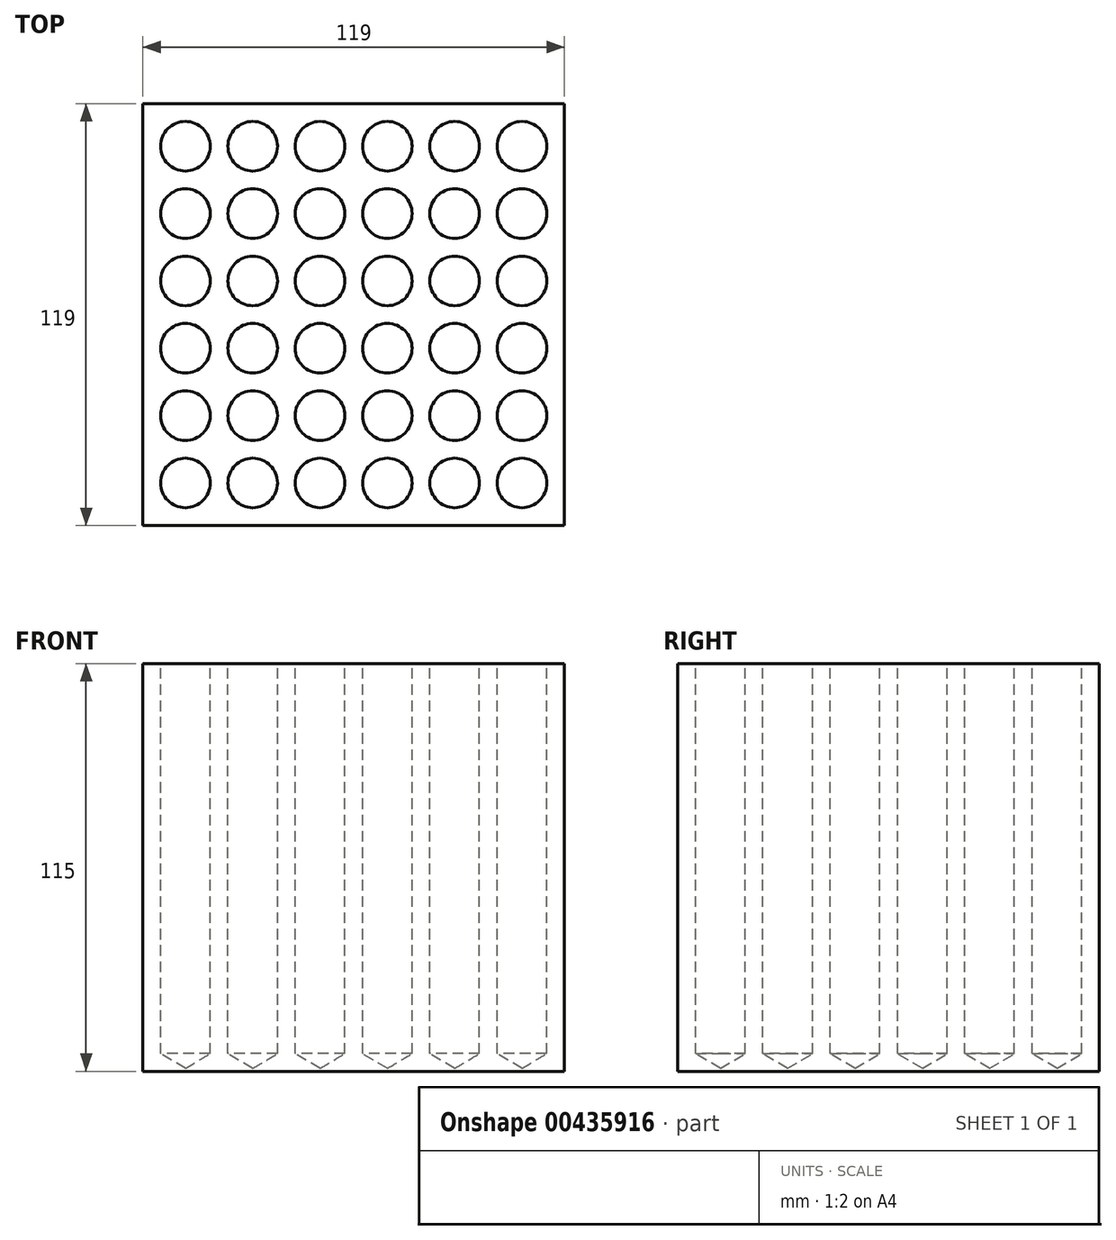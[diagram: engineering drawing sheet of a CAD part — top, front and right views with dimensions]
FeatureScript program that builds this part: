
annotation { "Feature Type Name" : "Feature", "Feature Type Description" : "" }
export const myFeature = defineFeature(function(context is Context, id is Id, definition is map)
    precondition{}
    {
        {
            var Q0;
            Q0=qCreatedBy(makeId("Top.planeOp"),FACE);
            var sketch = newSketch(context, id + "F0", { "sketchPlane" : qUnion([Q0])});
            skLineSegment(sketch, "E0.bottom", {"start": v(-97.3, 0) * mm, "end": v(21.7, 0) * mm});
            skLineSegment(sketch, "E0.top", {"start": v(-97.3, -119) * mm, "end": v(21.7, -119) * mm});
            skLineSegment(sketch, "E0.left", {"start": v(-97.3, 0) * mm, "end": v(-97.3, -119) * mm});
            skLineSegment(sketch, "E0.right", {"start": v(21.7, 0) * mm, "end": v(21.7, -119) * mm});
            skPoint(sketch, "E1", {"position": v(-85.3, -12) * mm});
            skPoint(sketch, "E2.0.1.0", {"position": v(-85.3, -31) * mm});
            skPoint(sketch, "E2.0.2.0", {"position": v(-85.3, -50) * mm});
            skPoint(sketch, "E2.0.3.0", {"position": v(-85.3, -69) * mm});
            skPoint(sketch, "E2.0.4.0", {"position": v(-85.3, -88) * mm});
            skPoint(sketch, "E2.0.5.0", {"position": v(-85.3, -107) * mm});
            skPoint(sketch, "E2.1.0.0", {"position": v(-66.3, -12) * mm});
            skPoint(sketch, "E2.1.1.0", {"position": v(-66.3, -31) * mm});
            skPoint(sketch, "E2.1.2.0", {"position": v(-66.3, -50) * mm});
            skPoint(sketch, "E2.1.3.0", {"position": v(-66.3, -69) * mm});
            skPoint(sketch, "E2.1.4.0", {"position": v(-66.3, -88) * mm});
            skPoint(sketch, "E2.1.5.0", {"position": v(-66.3, -107) * mm});
            skPoint(sketch, "E2.2.0.0", {"position": v(-47.3, -12) * mm});
            skPoint(sketch, "E2.2.1.0", {"position": v(-47.3, -31) * mm});
            skPoint(sketch, "E2.2.2.0", {"position": v(-47.3, -50) * mm});
            skPoint(sketch, "E2.2.3.0", {"position": v(-47.3, -69) * mm});
            skPoint(sketch, "E2.2.4.0", {"position": v(-47.3, -88) * mm});
            skPoint(sketch, "E2.2.5.0", {"position": v(-47.3, -107) * mm});
            skPoint(sketch, "E2.3.0.0", {"position": v(-28.3, -12) * mm});
            skPoint(sketch, "E2.3.1.0", {"position": v(-28.3, -31) * mm});
            skPoint(sketch, "E2.3.2.0", {"position": v(-28.3, -50) * mm});
            skPoint(sketch, "E2.3.3.0", {"position": v(-28.3, -69) * mm});
            skPoint(sketch, "E2.3.4.0", {"position": v(-28.3, -88) * mm});
            skPoint(sketch, "E2.3.5.0", {"position": v(-28.3, -107) * mm});
            skPoint(sketch, "E2.4.0.0", {"position": v(-9.3, -12) * mm});
            skPoint(sketch, "E2.4.1.0", {"position": v(-9.3, -31) * mm});
            skPoint(sketch, "E2.4.2.0", {"position": v(-9.3, -50) * mm});
            skPoint(sketch, "E2.4.3.0", {"position": v(-9.3, -69) * mm});
            skPoint(sketch, "E2.4.4.0", {"position": v(-9.3, -88) * mm});
            skPoint(sketch, "E2.4.5.0", {"position": v(-9.3, -107) * mm});
            skPoint(sketch, "E2.5.0.0", {"position": v(9.7, -12) * mm});
            skPoint(sketch, "E2.5.1.0", {"position": v(9.7, -31) * mm});
            skPoint(sketch, "E2.5.2.0", {"position": v(9.7, -50) * mm});
            skPoint(sketch, "E2.5.3.0", {"position": v(9.7, -69) * mm});
            skPoint(sketch, "E2.5.4.0", {"position": v(9.7, -88) * mm});
            skPoint(sketch, "E2.5.5.0", {"position": v(9.7, -107) * mm});
            skLineSegment(sketch, "E2.direction1", {"start": v(-85.3, -12) * mm, "end": v(-66.3, -12) * mm, "construction": true});
            skLineSegment(sketch, "E2.direction2", {"start": v(-85.3, -12) * mm, "end": v(-85.3, -31) * mm, "construction": true});
            skSolve(sketch);
        }
        {
            var Q0;
            Q0=makeQuery(id+"F0.imprint","IMPRINT",FACE,{"disambiguationData":[TD([[makeQuery(id+"F0.imprint","IMPRINT",EDGE,{"derivedFrom":sQuery(id+"F0.wireOp",EDGE,"E0.bottom")}),-1.0]])]});
            extrude(context, id + "F1", {"entities" : qUnion([Q0]), "oppositeDirection" : true, "depth" : 115 * mm});
        }
        {
            var Q0;
            Q0=sQuery(id+"F0.wireOp",VERTEX,"E1");
            var Q1;
            Q1=sQuery(id+"F0.wireOp",VERTEX,"E2.1.0.0");
            var Q2;
            Q2=sQuery(id+"F0.wireOp",VERTEX,"E2.2.0.0");
            var Q3;
            Q3=sQuery(id+"F0.wireOp",VERTEX,"E2.3.0.0");
            var Q4;
            Q4=sQuery(id+"F0.wireOp",VERTEX,"E2.4.0.0");
            var Q5;
            Q5=sQuery(id+"F0.wireOp",VERTEX,"E2.5.0.0");
            var Q6;
            Q6=sQuery(id+"F0.wireOp",VERTEX,"E2.5.1.0");
            var Q7;
            Q7=sQuery(id+"F0.wireOp",VERTEX,"E2.4.1.0");
            var Q8;
            Q8=sQuery(id+"F0.wireOp",VERTEX,"E2.3.1.0");
            var Q9;
            Q9=sQuery(id+"F0.wireOp",VERTEX,"E2.2.1.0");
            var Q10;
            Q10=sQuery(id+"F0.wireOp",VERTEX,"E2.1.1.0");
            var Q11;
            Q11=sQuery(id+"F0.wireOp",VERTEX,"E2.0.1.0");
            var Q12;
            Q12=sQuery(id+"F0.wireOp",VERTEX,"E2.0.2.0");
            var Q13;
            Q13=sQuery(id+"F0.wireOp",VERTEX,"E2.1.2.0");
            var Q14;
            Q14=sQuery(id+"F0.wireOp",VERTEX,"E2.2.2.0");
            var Q15;
            Q15=sQuery(id+"F0.wireOp",VERTEX,"E2.3.2.0");
            var Q16;
            Q16=sQuery(id+"F0.wireOp",VERTEX,"E2.4.2.0");
            var Q17;
            Q17=sQuery(id+"F0.wireOp",VERTEX,"E2.5.2.0");
            var Q18;
            Q18=sQuery(id+"F0.wireOp",VERTEX,"E2.5.3.0");
            var Q19;
            Q19=sQuery(id+"F0.wireOp",VERTEX,"E2.4.3.0");
            var Q20;
            Q20=sQuery(id+"F0.wireOp",VERTEX,"E2.3.3.0");
            var Q21;
            Q21=sQuery(id+"F0.wireOp",VERTEX,"E2.2.3.0");
            var Q22;
            Q22=sQuery(id+"F0.wireOp",VERTEX,"E2.1.3.0");
            var Q23;
            Q23=sQuery(id+"F0.wireOp",VERTEX,"E2.0.3.0");
            var Q24;
            Q24=sQuery(id+"F0.wireOp",VERTEX,"E2.0.4.0");
            var Q25;
            Q25=sQuery(id+"F0.wireOp",VERTEX,"E2.1.4.0");
            var Q26;
            Q26=sQuery(id+"F0.wireOp",VERTEX,"E2.2.4.0");
            var Q27;
            Q27=sQuery(id+"F0.wireOp",VERTEX,"E2.3.4.0");
            var Q28;
            Q28=sQuery(id+"F0.wireOp",VERTEX,"E2.4.4.0");
            var Q29;
            Q29=sQuery(id+"F0.wireOp",VERTEX,"E2.5.4.0");
            var Q30;
            Q30=sQuery(id+"F0.wireOp",VERTEX,"E2.5.5.0");
            var Q31;
            Q31=sQuery(id+"F0.wireOp",VERTEX,"E2.4.5.0");
            var Q32;
            Q32=sQuery(id+"F0.wireOp",VERTEX,"E2.3.5.0");
            var Q33;
            Q33=sQuery(id+"F0.wireOp",VERTEX,"E2.2.5.0");
            var Q34;
            Q34=sQuery(id+"F0.wireOp",VERTEX,"E2.1.5.0");
            var Q35;
            Q35=sQuery(id+"F0.wireOp",VERTEX,"E2.0.5.0");
            var Q36;
            Q36=makeQuery(id+"F1.opExtrude","SWEPT_BODY",BODY,{"disambiguationData":[OSD([sQuery(id+"F0.wireOp",EDGE,"E0.bottom"),sQuery(id+"F0.wireOp",EDGE,"E0.top"),sQuery(id+"F0.wireOp",EDGE,"E0.left"),sQuery(id+"F0.wireOp",EDGE,"E0.right")])]});
            hole(context, id + "F2", {"style" : HoleStyle.SIMPLE, "endStyle" : HoleEndStyle.BLIND, "holeDiameter" : 14 * mm, "holeDepth" : 110 * mm, "isTappedThrough" : true, "tappedDepth" : 12 * mm, "tapClearance" : 3, "locations" : qUnion([Q0, Q1, Q2, Q3, Q4, Q5, Q6, Q7, Q8, Q9, Q10, Q11, Q12, Q13, Q14, Q15, Q16, Q17, Q18, Q19, Q20, Q21, Q22, Q23, Q24, Q25, Q26, Q27, Q28, Q29, Q30, Q31, Q32, Q33, Q34, Q35]), "scope" : qUnion([Q36])});
        }
    });
